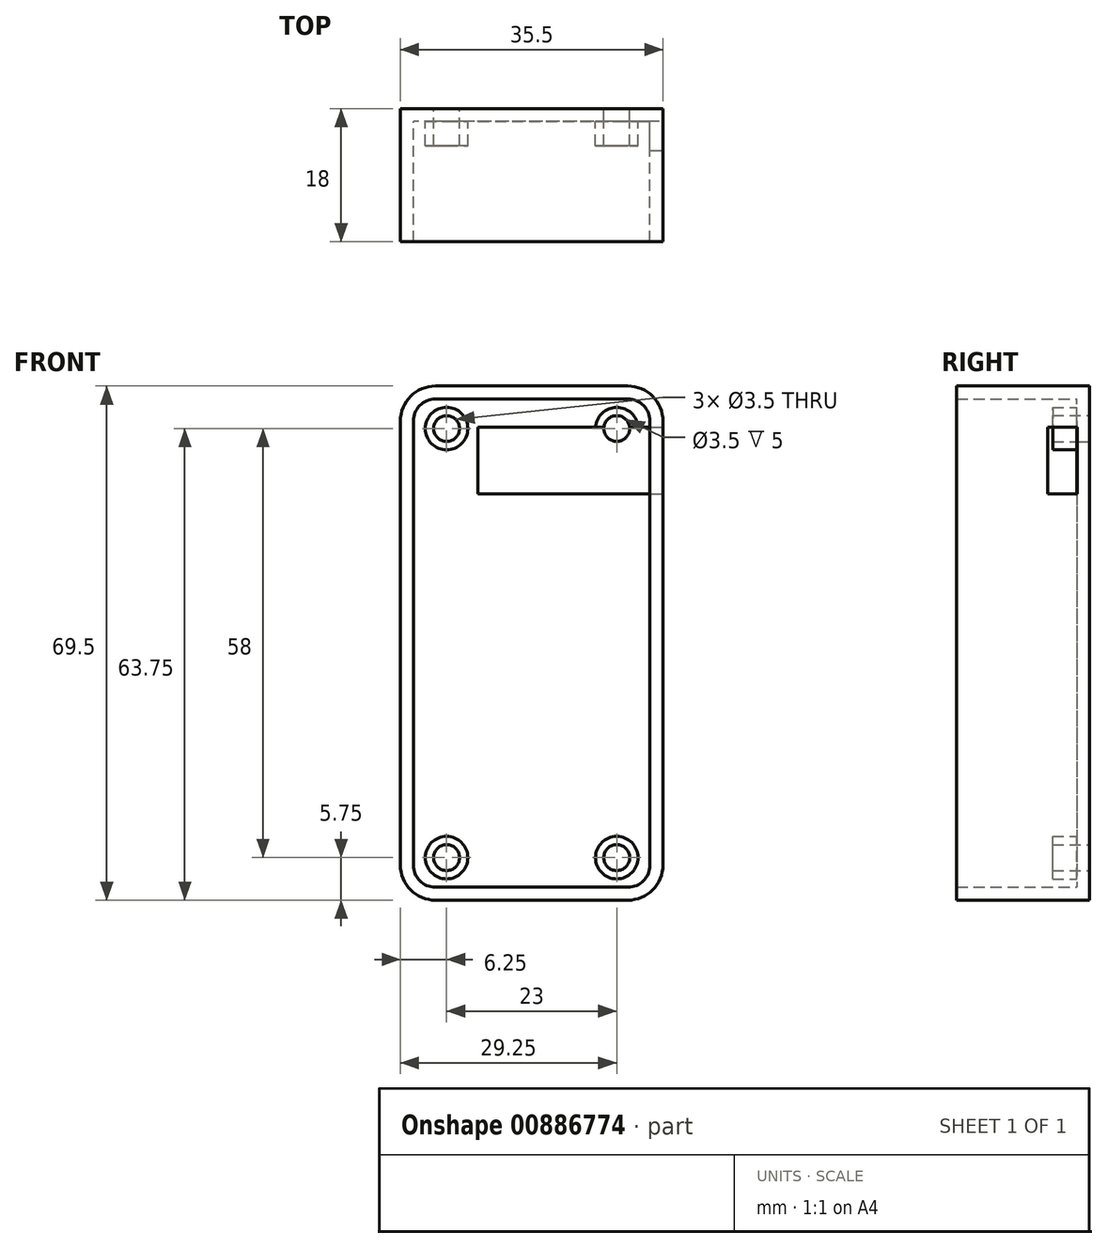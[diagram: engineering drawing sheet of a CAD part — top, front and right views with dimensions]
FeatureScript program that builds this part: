
annotation { "Feature Type Name" : "Feature", "Feature Type Description" : "" }
export const myFeature = defineFeature(function(context is Context, id is Id, definition is map)
    precondition{}
    {
        {
            var Q0;
            Q0=qCreatedBy(makeId("Front.planeOp"),FACE);
            var sketch = newSketch(context, id + "F0", { "sketchPlane" : qUnion([Q0])});
            skPoint(sketch, "E0.middle", {"position": v(0, 0) * mm});
            skCircle(sketch, "E1", {"center": v(-11.5, 29) * mm, "radius": 1.75 * mm});
            skCircle(sketch, "E2", {"center": v(11.5, 29) * mm, "radius": 1.75 * mm});
            skCircle(sketch, "E3", {"center": v(11.5, -29) * mm, "radius": 1.75 * mm});
            skCircle(sketch, "E4", {"center": v(-11.5, -29) * mm, "radius": 1.75 * mm});
            skCircle(sketch, "E5", {"center": v(-11.5, 29) * mm, "radius": 2.88 * mm});
            skCircle(sketch, "E6", {"center": v(11.5, 29) * mm, "radius": 2.88 * mm});
            skCircle(sketch, "E7", {"center": v(11.5, -29) * mm, "radius": 2.88 * mm});
            skCircle(sketch, "E8", {"center": v(-11.5, -29) * mm, "radius": 2.88 * mm});
            skLineSegment(sketch, "E9.0", {"start": v(-16, 30) * mm, "end": v(-16, -30) * mm});
            skLineSegment(sketch, "E9.1", {"start": v(13, 33) * mm, "end": v(-13, 33) * mm});
            skLineSegment(sketch, "E9.2", {"start": v(16, 30) * mm, "end": v(16, -30) * mm});
            skLineSegment(sketch, "E9.3", {"start": v(13, -33) * mm, "end": v(-13, -33) * mm});
            skPoint(sketch, "E10.visualSharp", {"position": v(-16, -33) * mm});
            skArc(sketch, "E10.filletArc", {"start": v(-16, -30) * mm, "mid": v(-15.12, -32.12) * mm, "end": v(-13, -33) * mm});
            skPoint(sketch, "E11.visualSharp", {"position": v(16, -33) * mm});
            skArc(sketch, "E11.filletArc", {"start": v(13, -33) * mm, "mid": v(15.12, -32.12) * mm, "end": v(16, -30) * mm});
            skPoint(sketch, "E12.visualSharp", {"position": v(16, 33) * mm});
            skArc(sketch, "E12.filletArc", {"start": v(16, 30) * mm, "mid": v(15.12, 32.12) * mm, "end": v(13, 33) * mm});
            skPoint(sketch, "E13.visualSharp", {"position": v(-16, 33) * mm});
            skArc(sketch, "E13.filletArc", {"start": v(-13, 33) * mm, "mid": v(-15.12, 32.12) * mm, "end": v(-16, 30) * mm});
            skArc(sketch, "E14.0", {"start": v(-13, 34.75) * mm, "mid": v(-16.36, 33.36) * mm, "end": v(-17.75, 30) * mm});
            skLineSegment(sketch, "E14.1", {"start": v(13, 34.75) * mm, "end": v(-13, 34.75) * mm});
            skLineSegment(sketch, "E14.2", {"start": v(-17.75, 30) * mm, "end": v(-17.75, -30) * mm});
            skArc(sketch, "E14.3", {"start": v(17.75, 30) * mm, "mid": v(16.36, 33.36) * mm, "end": v(13, 34.75) * mm});
            skArc(sketch, "E14.4", {"start": v(-17.75, -30) * mm, "mid": v(-16.36, -33.36) * mm, "end": v(-13, -34.75) * mm});
            skLineSegment(sketch, "E14.5", {"start": v(13, -34.75) * mm, "end": v(-13, -34.75) * mm});
            skArc(sketch, "E14.6", {"start": v(13, -34.75) * mm, "mid": v(16.36, -33.36) * mm, "end": v(17.75, -30) * mm});
            skLineSegment(sketch, "E14.7", {"start": v(17.75, 30) * mm, "end": v(17.75, -30) * mm});
            skSolve(sketch);
        }
        {
            var Q0;
            Q0=makeQuery(id+"F0.imprint","IMPRINT",FACE,{"disambiguationData":[TD([[makeQuery(id+"F0.imprint","IMPRINT",EDGE,{"derivedFrom":sQuery(id+"F0.wireOp",EDGE,"E5")}),-1.0]])]});
            extrude(context, id + "F1", {"entities" : qUnion([Q0]), "depth" : 1.75 * mm, "offsetDistance" : 25 * mm});
        }
        {
            var Q0;
            Q0 = qSketchRegion(id + "F0", true);
            extrude(context, id + "F2", {"entities" : qUnion([Q0]), "operationType" : NewBodyOperationType.ADD, "depth" : 18 * mm, "offsetDistance" : 25 * mm});
        }
        {
            var Q0;
            Q0=makeQuery(id+"F0.imprint","IMPRINT",FACE,{"disambiguationData":[TD([[makeQuery(id+"F0.imprint","IMPRINT",EDGE,{"derivedFrom":sQuery(id+"F0.wireOp",EDGE,"E1")}),-1.0]])]});
            var Q1;
            Q1=makeQuery(id+"F0.imprint","IMPRINT",FACE,{"disambiguationData":[TD([[makeQuery(id+"F0.imprint","IMPRINT",EDGE,{"derivedFrom":sQuery(id+"F0.wireOp",EDGE,"E2")}),-1.0]])]});
            var Q2;
            Q2=makeQuery(id+"F0.imprint","IMPRINT",FACE,{"disambiguationData":[TD([[makeQuery(id+"F0.imprint","IMPRINT",EDGE,{"derivedFrom":sQuery(id+"F0.wireOp",EDGE,"E3")}),-1.0]])]});
            var Q3;
            Q3=makeQuery(id+"F0.imprint","IMPRINT",FACE,{"disambiguationData":[TD([[makeQuery(id+"F0.imprint","IMPRINT",EDGE,{"derivedFrom":sQuery(id+"F0.wireOp",EDGE,"E4")}),-1.0]])]});
            var Q4;
            Q4=sQuery(id+"F0.wireOp",EDGE,"E5");
            var Q5;
            Q5=sQuery(id+"F0.wireOp",EDGE,"E1");
            extrude(context, id + "F3", {"entities" : qUnion([Q0, Q1, Q2, Q3]), "operationType" : NewBodyOperationType.ADD, "surfaceEntities" : qUnion([Q4, Q5]), "depth" : 5 * mm, "offsetDistance" : 25 * mm});
        }
        {
            var Q0;
            Q0=makeQuery(id+"F2.opExtrude","SWEPT_FACE",FACE,{"disambiguationData":[OSD([sQuery(id+"F0.wireOp",EDGE,"E14.7")])]});
            var sketch = newSketch(context, id + "F4", { "sketchPlane" : qUnion([Q0])});
            skLineSegment(sketch, "E15.bottom", {"start": v(-5.66, 29.16) * mm, "end": v(-1.66, 29.16) * mm});
            skLineSegment(sketch, "E15.top", {"start": v(-5.66, 20.16) * mm, "end": v(-1.66, 20.16) * mm});
            skLineSegment(sketch, "E15.left", {"start": v(-5.66, 29.16) * mm, "end": v(-5.66, 20.16) * mm});
            skLineSegment(sketch, "E15.right", {"start": v(-1.66, 29.16) * mm, "end": v(-1.66, 20.16) * mm});
            skSolve(sketch);
        }
        {
            var Q0;
            Q0 = qSketchRegion(id + "F4", true);
            extrude(context, id + "F5", {"entities" : qUnion([Q0]), "operationType" : NewBodyOperationType.REMOVE, "oppositeDirection" : true, "depth" : 25 * mm, "offsetDistance" : 25 * mm});
        }
    });
